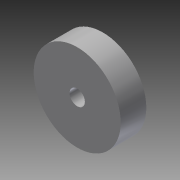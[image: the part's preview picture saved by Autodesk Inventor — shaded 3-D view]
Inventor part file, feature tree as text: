
AUTODESK INVENTOR PART (.ipt)
format: ipt  version: 2013 (Build 170138000, 138)  size: 79,872 bytes
history: native  units: in
note: dims shown in document units (in); Inventor stores cm internally (conversion verified against a paired STEP export)
features: extrude x2, sketch x2
ambient origin geometry x8: Origin, YZ Plane, XZ Plane, XY Plane, X Axis, Y Axis, Z Axis, Center Point
bodies: Solid1 (feature_tree)
feature tree (4):
  extrude  "Extrusion1"  Depth=0.3125in TaperAngle=0.0deg
  extrude  "Extrusion2"  Depth=1.0in TaperAngle=0.0deg
  sketch  "Sketch1"  dims[d0=1.0625in d2=0.3125in d3=0.0in]
  sketch  "Sketch2"  dims[d4=0.1875in d5=1.0in d6=0.0in]
